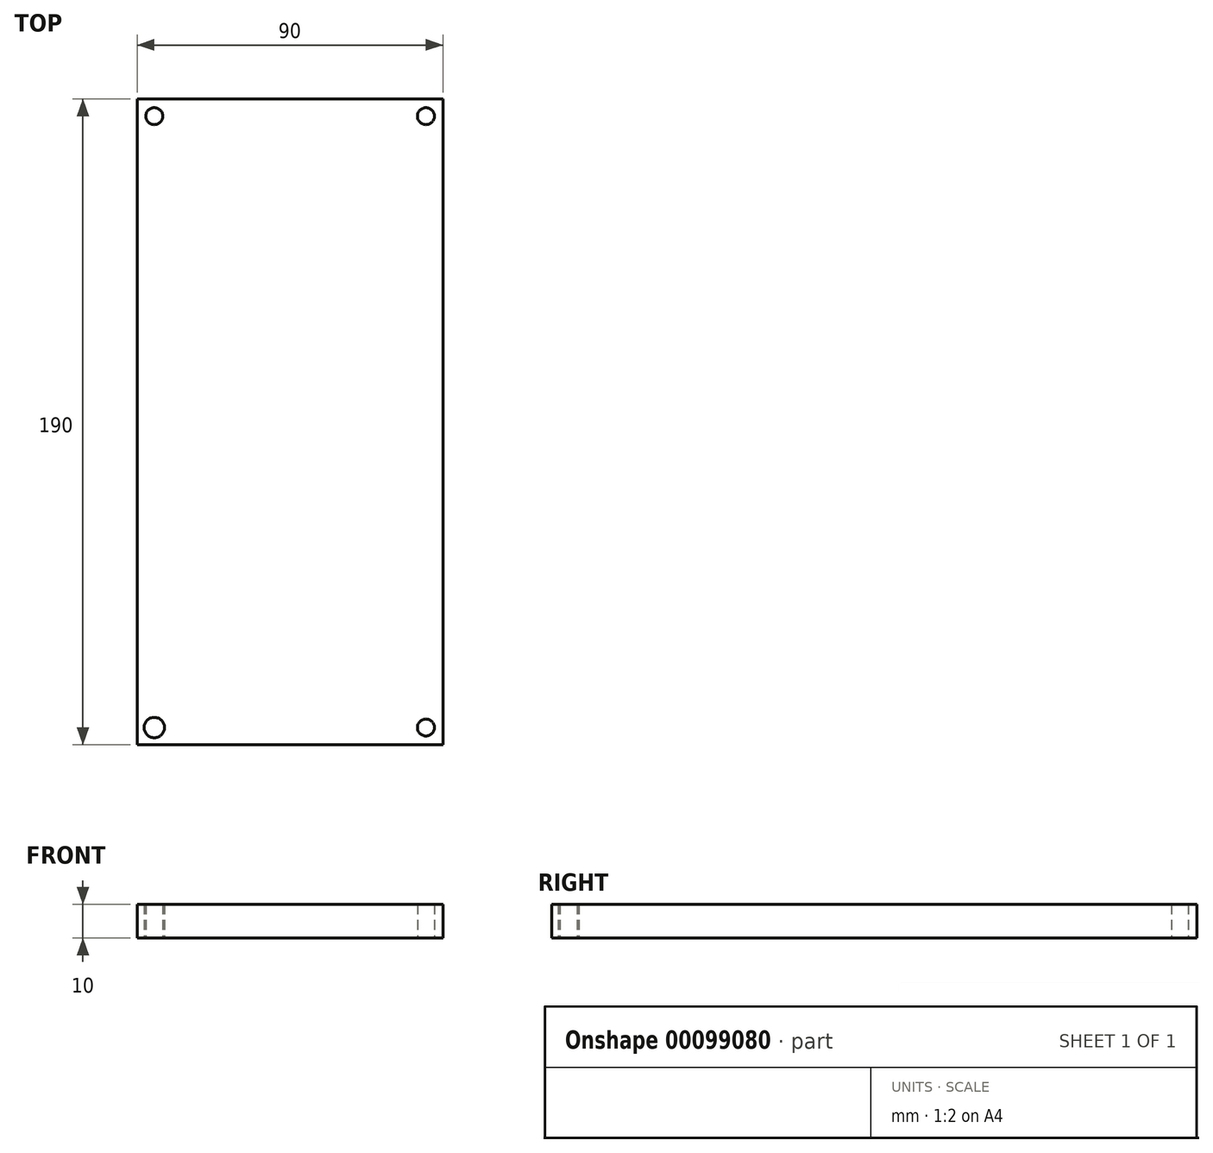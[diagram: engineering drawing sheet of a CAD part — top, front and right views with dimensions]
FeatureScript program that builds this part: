
annotation { "Feature Type Name" : "Feature", "Feature Type Description" : "" }
export const myFeature = defineFeature(function(context is Context, id is Id, definition is map)
    precondition{}
    {
        {
            var Q0;
            Q0=qCreatedBy(makeId("Top.planeOp"),FACE);
            var sketch = newSketch(context, id + "F0", { "sketchPlane" : qUnion([Q0])});
            skLineSegment(sketch, "E0.bottom", {"start": v(-39.9, 181.17) * mm, "end": v(50.1, 181.17) * mm});
            skLineSegment(sketch, "E0.top", {"start": v(-39.9, -8.83) * mm, "end": v(50.1, -8.83) * mm});
            skLineSegment(sketch, "E0.left", {"start": v(-39.9, 181.17) * mm, "end": v(-39.9, -8.83) * mm});
            skLineSegment(sketch, "E0.right", {"start": v(50.1, 181.17) * mm, "end": v(50.1, -8.83) * mm});
            skCircle(sketch, "E1", {"center": v(-34.9, -3.83) * mm, "radius": 3 * mm});
            skCircle(sketch, "E2", {"center": v(-34.9, 176.17) * mm, "radius": 2.5 * mm});
            skCircle(sketch, "E3", {"center": v(45.1, 176.17) * mm, "radius": 2.5 * mm});
            skCircle(sketch, "E4", {"center": v(45.1, -3.83) * mm, "radius": 2.5 * mm});
            skSolve(sketch);
        }
        {
            var Q0;
            Q0 = qSketchRegion(id + "F0", true);
            extrude(context, id + "F1", {"entities" : qUnion([Q0]), "depth" : 10 * mm});
        }
    });
